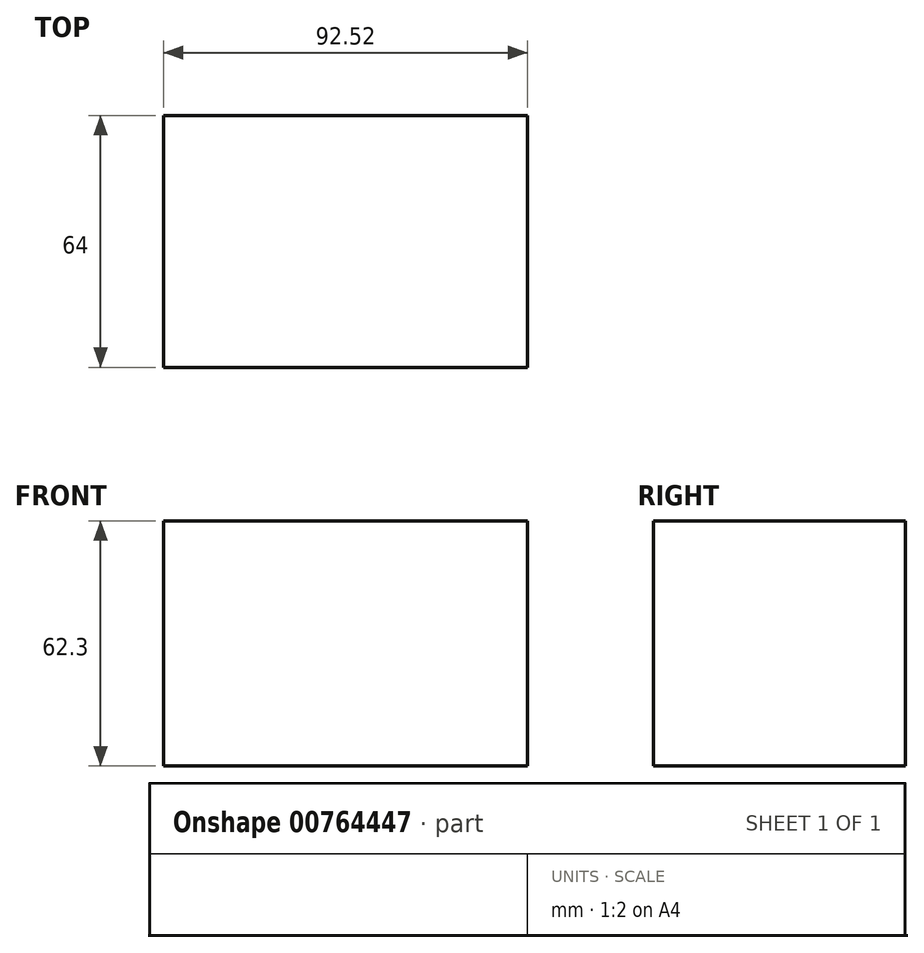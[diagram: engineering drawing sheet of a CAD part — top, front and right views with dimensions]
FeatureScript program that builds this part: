
annotation { "Feature Type Name" : "Feature", "Feature Type Description" : "" }
export const myFeature = defineFeature(function(context is Context, id is Id, definition is map)
    precondition{}
    {
        {
            var Q0;
            Q0=qCreatedBy(makeId("Top.planeOp"),FACE);
            var sketch = newSketch(context, id + "F0", { "sketchPlane" : qUnion([Q0])});
            skLineSegment(sketch, "E0.bottom", {"start": v(-46.26, 32) * mm, "end": v(46.26, 32) * mm});
            skLineSegment(sketch, "E0.top", {"start": v(-46.26, -32) * mm, "end": v(46.26, -32) * mm});
            skLineSegment(sketch, "E0.left", {"start": v(-46.26, 32) * mm, "end": v(-46.26, -32) * mm});
            skLineSegment(sketch, "E0.right", {"start": v(46.26, 32) * mm, "end": v(46.26, -32) * mm});
            skPoint(sketch, "E0.middle", {"position": v(0, 0) * mm});
            skSolve(sketch);
        }
        {
            var Q0;
            Q0 = qSketchRegion(id + "F0", true);
            extrude(context, id + "F1", {"entities" : qUnion([Q0]), "oppositeDirection" : true, "depth" : 62.3 * mm, "offsetDistance" : 25 * mm});
        }
    });
